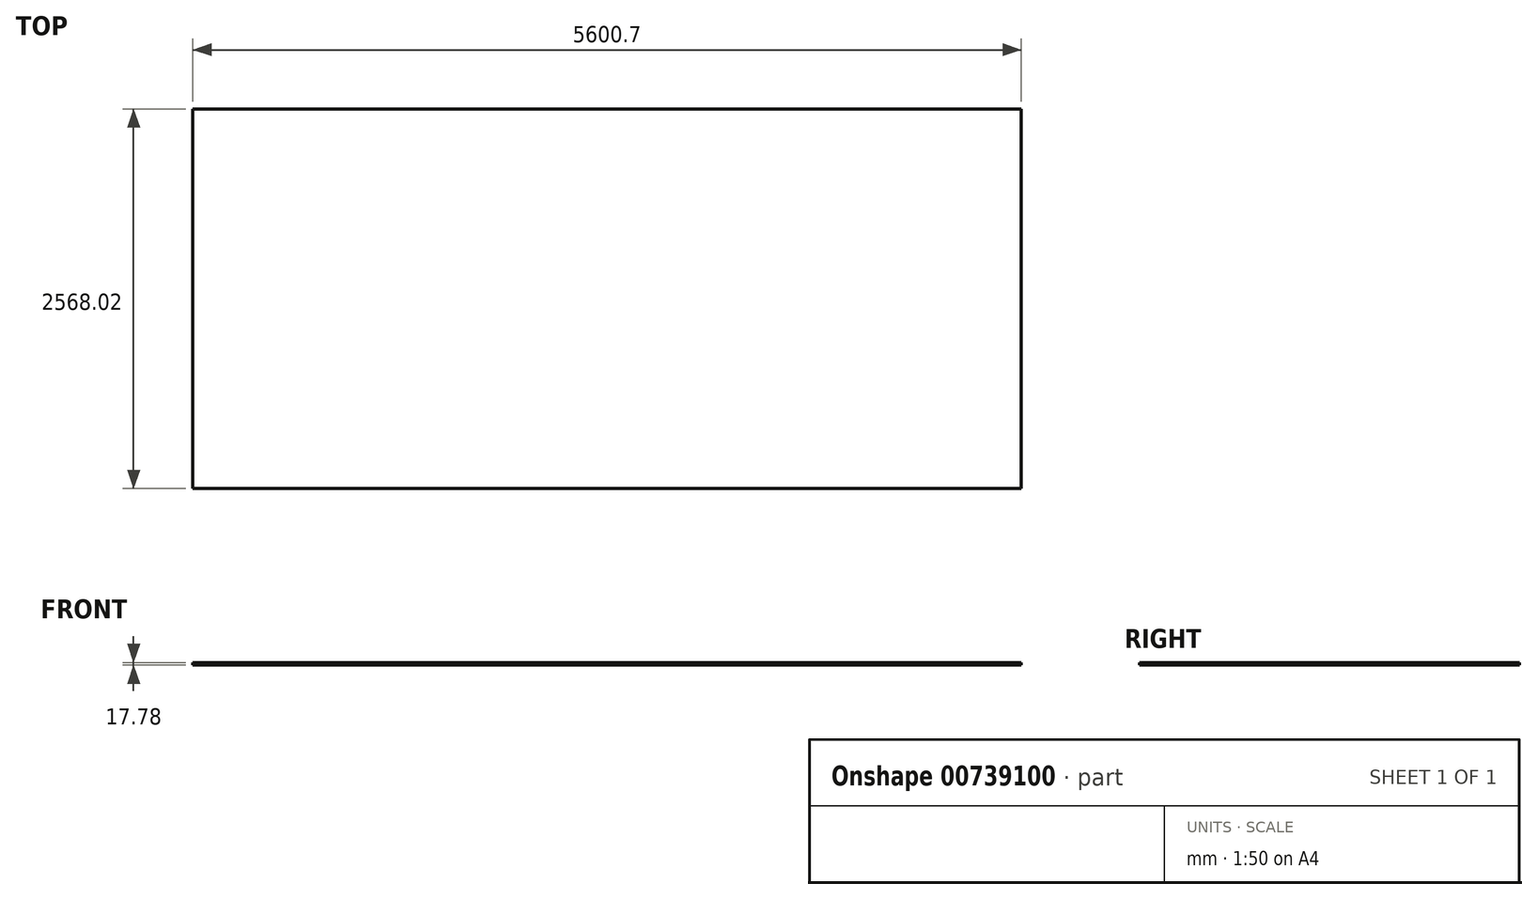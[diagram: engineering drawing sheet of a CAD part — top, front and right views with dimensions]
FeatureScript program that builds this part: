
annotation { "Feature Type Name" : "Feature", "Feature Type Description" : "" }
export const myFeature = defineFeature(function(context is Context, id is Id, definition is map)
    precondition{}
    {
        {
            var Q0;
            Q0=qCreatedBy(makeId("Top.planeOp"),FACE);
            var sketch = newSketch(context, id + "F0", { "sketchPlane" : qUnion([Q0])});
            skLineSegment(sketch, "E0.bottom", {"start": v(0, 0) * mm, "end": v(5600.7, 0) * mm});
            skLineSegment(sketch, "E0.top", {"start": v(0, 2568.02) * mm, "end": v(5600.7, 2568.02) * mm});
            skLineSegment(sketch, "E0.left", {"start": v(0, 0) * mm, "end": v(0, 2568.02) * mm});
            skLineSegment(sketch, "E0.right", {"start": v(5600.7, 0) * mm, "end": v(5600.7, 2568.02) * mm});
            skSolve(sketch);
        }
        {
            var Q0;
            Q0=makeQuery(id+"F0.imprint","IMPRINT",FACE,{"disambiguationData":[TD([[makeQuery(id+"F0.imprint","IMPRINT",EDGE,{"derivedFrom":sQuery(id+"F0.wireOp",EDGE,"E0.bottom")}),1.0]])]});
            extrude(context, id + "F1", {"entities" : qUnion([Q0]), "depth" : 17.78 * mm, "offsetDistance" : 25.4 * mm});
        }
    });
